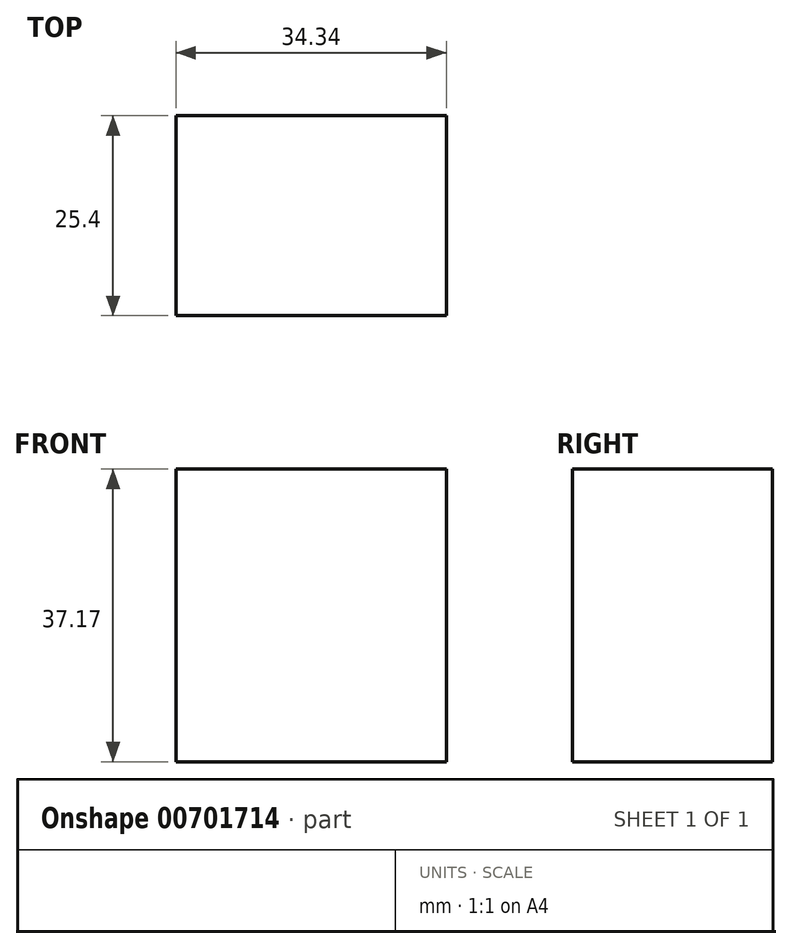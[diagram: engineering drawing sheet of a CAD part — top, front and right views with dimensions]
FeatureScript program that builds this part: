
annotation { "Feature Type Name" : "Feature", "Feature Type Description" : "" }
export const myFeature = defineFeature(function(context is Context, id is Id, definition is map)
    precondition{}
    {
        {
            var Q0;
            Q0=qCreatedBy(makeId("Front.planeOp"),FACE);
            var sketch = newSketch(context, id + "F0", { "sketchPlane" : qUnion([Q0])});
            skLineSegment(sketch, "E0", {"start": v(-63.12, 18.2) * mm, "end": v(-63.12, 55.38) * mm});
            skLineSegment(sketch, "E1", {"start": v(-63.12, 55.38) * mm, "end": v(-28.78, 55.38) * mm});
            skLineSegment(sketch, "E2", {"start": v(-28.78, 55.38) * mm, "end": v(-28.78, 18.2) * mm});
            skLineSegment(sketch, "E3", {"start": v(-28.78, 18.2) * mm, "end": v(-63.12, 18.2) * mm});
            skSolve(sketch);
        }
        {
            var Q0;
            Q0 = qSketchRegion(id + "F0", true);
            extrude(context, id + "F1", {"entities" : qUnion([Q0]), "depth" : 25.4 * mm, "offsetDistance" : 25.4 * mm});
        }
    });
